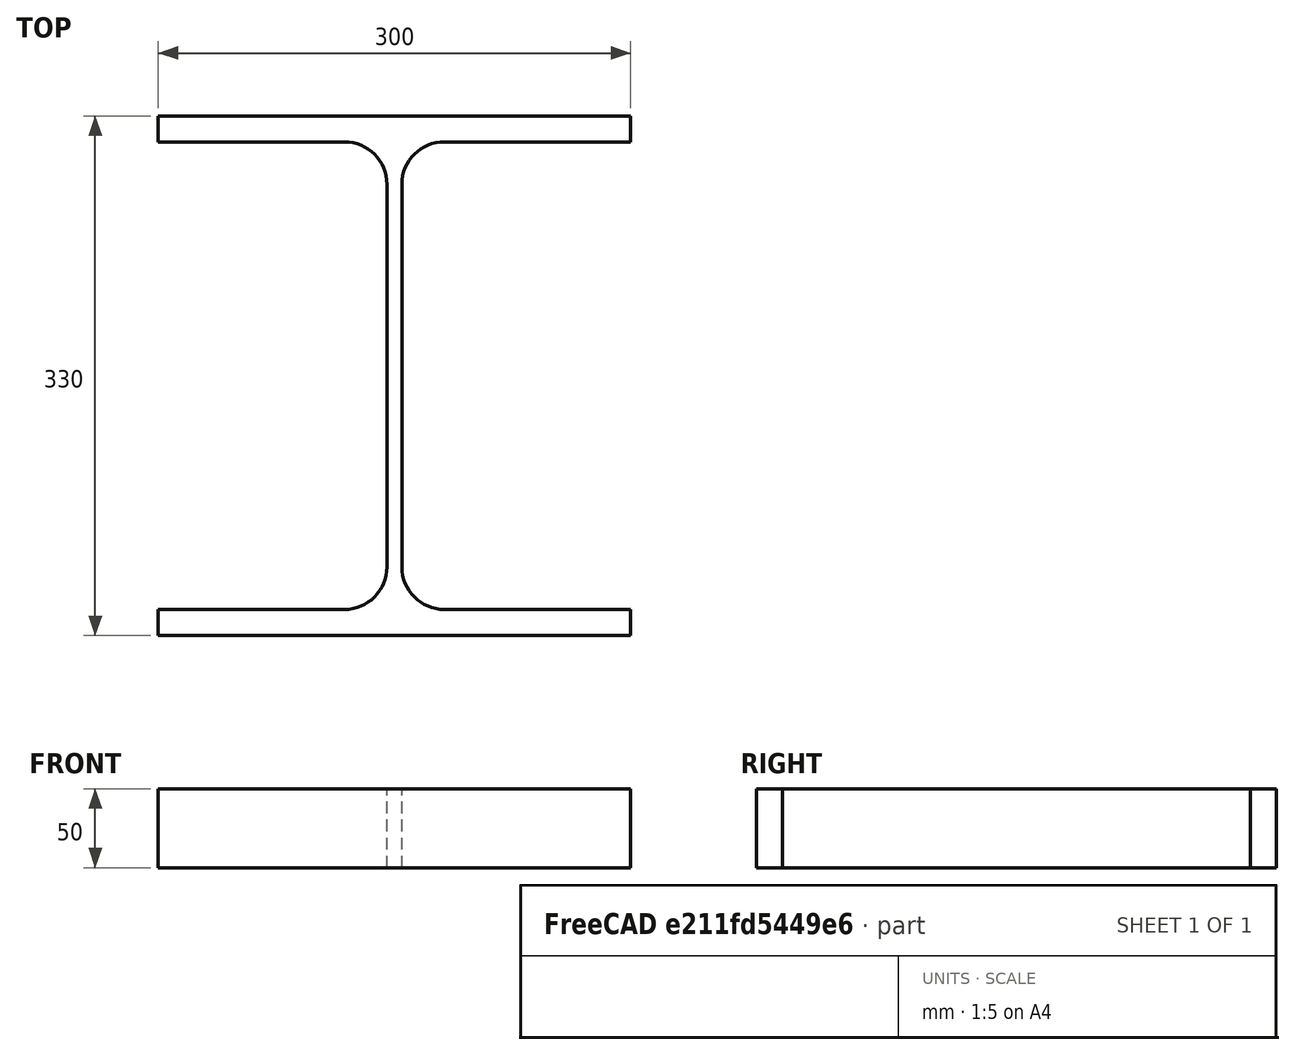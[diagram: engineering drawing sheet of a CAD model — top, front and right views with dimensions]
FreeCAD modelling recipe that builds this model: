
FCSTD DOCUMENT  (FreeCAD 0.15R4671 (Git))
Label: HE-A-Profile 340 DIN1025-3 S235JR
License: All rights reserved
LicenseURL: http://en.wikipedia.org/wiki/All_rights_reserved
objects: Sketcher::SketchObject×1, Part::Extrusion×1
note: 2 computed .brp shape members not serialized (recipe doc carries the construction recipe); baked Part::Feature solids carry a one-line shape summary decoded from their .brp

FEATURE [Sketcher::SketchObject] Sketch
  sketch-geometry (16):
    g0: LineSegment StartX=4.75 StartY=-121.5 StartZ=0 EndX=4.75 EndY=121.5 EndZ=0
    g1: LineSegment StartX=31.75 StartY=148.5 StartZ=0 EndX=150 EndY=148.5 EndZ=0
    g2: LineSegment StartX=150 StartY=148.5 StartZ=0 EndX=150 EndY=165 EndZ=0
    g3: LineSegment StartX=150 StartY=165 StartZ=0 EndX=-150 EndY=165 EndZ=0
    g4: LineSegment StartX=-150 StartY=165 StartZ=0 EndX=-150 EndY=148.5 EndZ=0
    g5: LineSegment StartX=-150 StartY=148.5 StartZ=0 EndX=-31.75 EndY=148.5 EndZ=0
    g6: LineSegment StartX=-4.75 StartY=121.5 StartZ=0 EndX=-4.75 EndY=-121.5 EndZ=0
    g7: LineSegment StartX=-31.75 StartY=-148.5 StartZ=0 EndX=-150 EndY=-148.5 EndZ=0
    g8: LineSegment StartX=-150 StartY=-148.5 StartZ=0 EndX=-150 EndY=-165 EndZ=0
    g9: LineSegment StartX=-150 StartY=-165 StartZ=0 EndX=150 EndY=-165 EndZ=0
    g10: LineSegment StartX=150 StartY=-165 StartZ=0 EndX=150 EndY=-148.5 EndZ=0
    g11: LineSegment StartX=150 StartY=-148.5 StartZ=0 EndX=31.75 EndY=-148.5 EndZ=0
    g12: ArcOfCircle CenterX=31.75 CenterY=121.5 CenterZ=0 NormalX=0 NormalY=0 NormalZ=1 Radius=27 StartAngle=1.5708 EndAngle=3.14159
    g13: ArcOfCircle CenterX=31.75 CenterY=-121.5 CenterZ=0 NormalX=0 NormalY=0 NormalZ=1 Radius=27 StartAngle=3.14159 EndAngle=4.71239
    g14: ArcOfCircle CenterX=-31.75 CenterY=121.5 CenterZ=0 NormalX=0 NormalY=0 NormalZ=1 Radius=27 StartAngle=0 EndAngle=1.5708
    g15: ArcOfCircle CenterX=-31.75 CenterY=-121.5 CenterZ=0 NormalX=0 NormalY=0 NormalZ=1 Radius=27 StartAngle=4.71239 EndAngle=6.28319
  constraints (42):
    c: Vertical(g0)
    c: Coincident(g2,g1)
    c: Vertical(g2)
    c: Coincident(g3,g2)
    c: Coincident(g4,g3)
    c: Vertical(g4)
    c: Coincident(g5,g4)
    c: Horizontal(g5)
    c: Vertical(g6)
    c: Horizontal(g7)
    c: Coincident(g8,g7)
    c: Vertical(g8)
    c: Coincident(g9,g8)
    c: Horizontal(g9)
    c: Coincident(g10,g9)
    c: Vertical(g10)
    c: Coincident(g11,g10)
    c: Horizontal(g11)
    c: Tangent(g1,g12) = 1.5708
    c: Tangent(g0,g12) = 1.5708
    c: Tangent(g0,g13) = 1.5708
    c: Tangent(g11,g13) = 1.5708
    c: Tangent(g5,g14) = 1.5708
    c: Tangent(g6,g14) = 1.5708
    c: Tangent(g6,g15) = 1.5708
    c: Tangent(g7,g15) = 1.5708
    c: Equal(g3,g9)
    c: Equal(g2,g4)
    c: Equal(g4,g8)
    c: Equal(g8,g10)
    c: Equal(g12,g14)
    c: Equal(g14,g15)
    c: Equal(g15,g13)
    c: Symmetric(g2,g3,g-2)
    c: Symmetric(g9,g8,g-2)
    c: Symmetric(g0,g6,g-2)
    c: Symmetric(g2,g9,g-1)
    c: DistanceY(g2,g9) = -330
    c: DistanceX(g3) = -300
    c: DistanceX(g0,g6) = -9.5
    c: DistanceY(g2) = 16.5
    c: Radius(g12) = 27
FEATURE [Part::Extrusion] Extrude  label="HE-A-Profile 340 DIN1025-3 S235JR"
  Base = -> Sketch
  Dir = (0,0,50)
  Solid = true
